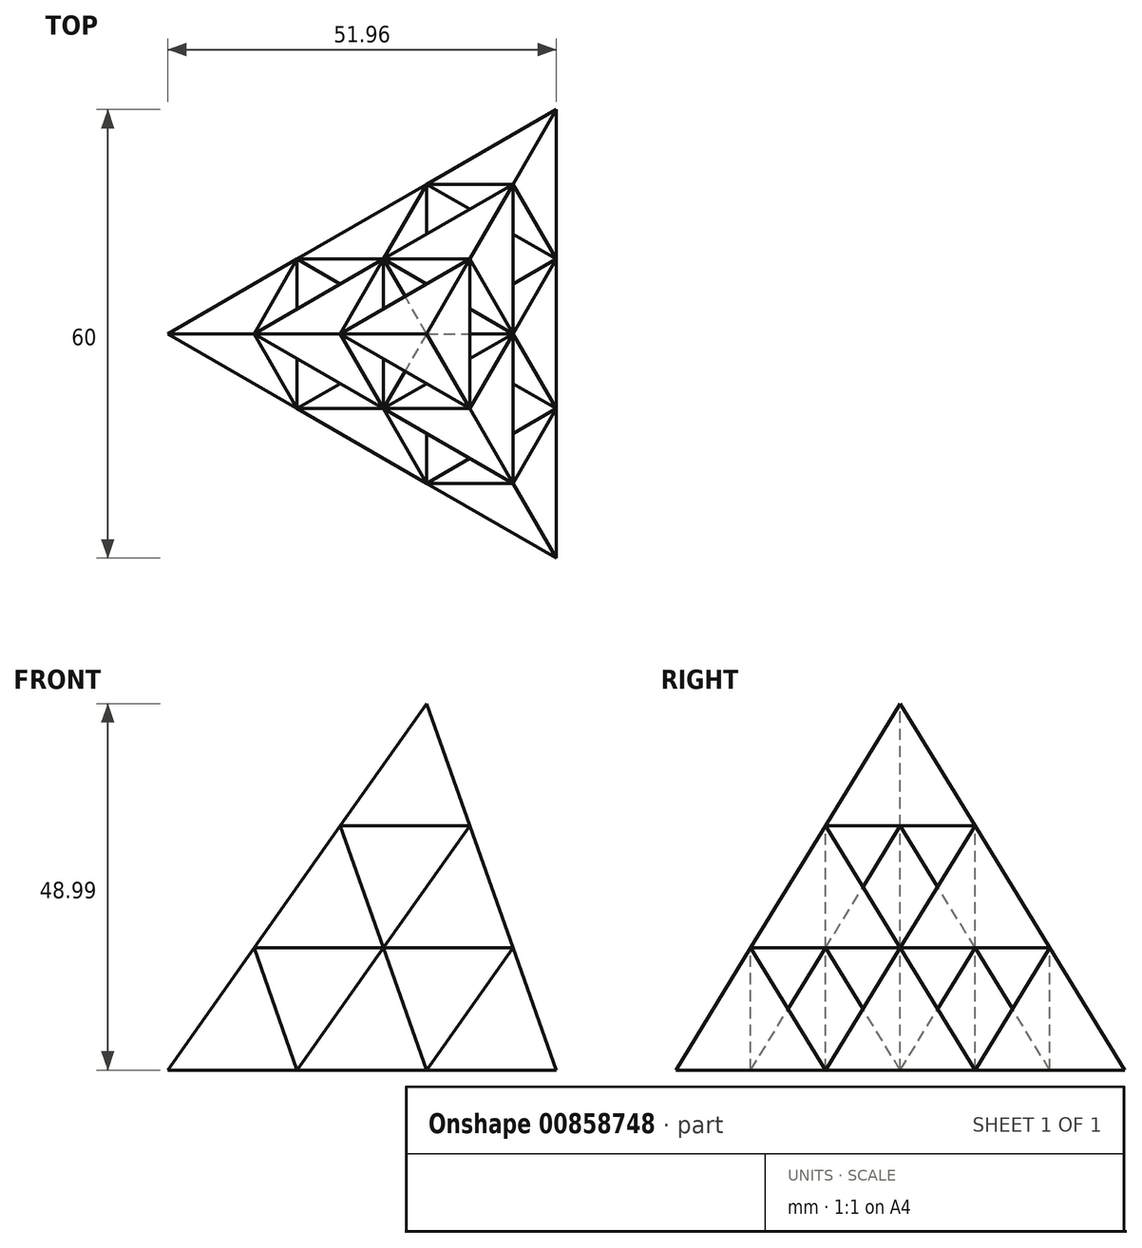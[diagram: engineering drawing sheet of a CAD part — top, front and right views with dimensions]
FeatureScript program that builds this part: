
annotation { "Feature Type Name" : "Feature", "Feature Type Description" : "" }
export const myFeature = defineFeature(function(context is Context, id is Id, definition is map)
    precondition{}
    {
        {
            var Q0;
            Q0=qCreatedBy(makeId("Top.planeOp"),FACE);
            var sketch = newSketch(context, id + "F0", { "sketchPlane" : qUnion([Q0])});
            skCircle(sketch, "E0.cCircle", {"center": v(0, 0) * mm, "radius": 5.77 * mm, "construction": true});
            skLineSegment(sketch, "E0.0", {"start": v(5.77, 10) * mm, "end": v(5.77, -10) * mm});
            skLineSegment(sketch, "E0.1", {"start": v(5.77, -10) * mm, "end": v(-11.55, 0) * mm});
            skLineSegment(sketch, "E0.2", {"start": v(-11.55, 0) * mm, "end": v(5.77, 10) * mm});
            skPoint(sketch, "E0.0.midPoint", {"position": v(5.77, 0) * mm});
            skSolve(sketch);
        }
        {
            var Q0;
            Q0=qCreatedBy(makeId("Front.planeOp"),FACE);
            var sketch = newSketch(context, id + "F1", { "sketchPlane" : qUnion([Q0])});
            skLineSegment(sketch, "E1", {"start": v(-11.55, 0) * mm, "end": v(0, 16.33) * mm});
            skSolve(sketch);
        }
        {
            var Q0;
            Q0=makeQuery(id+"F0.imprint","IMPRINT",FACE,{"disambiguationData":[TD([[makeQuery(id+"F0.imprint","IMPRINT",EDGE,{"derivedFrom":sQuery(id+"F0.wireOp",EDGE,"E0.0")}),-1.0]])]});
            var Q1;
            Q1=sQuery(id+"F1.wireOp",VERTEX,"E1.end");
            loft(context, id + "F2", {"sheetProfilesArray" : [{ "sheetProfileEntities" : qUnion([Q0]) }, { "sheetProfileEntities" : qUnion([Q1]) }]});
        }
        {
            var Q0;
            Q0=makeQuery(id+"F2.opLoft","SWEPT_BODY",BODY,{"disambiguationData":[OSD([makeQuery(id+"F0.imprint","IMPRINT",FACE,{"disambiguationData":[TD([[makeQuery(id+"F0.imprint","IMPRINT",EDGE,{"derivedFrom":sQuery(id+"F0.wireOp",EDGE,"E0.0")}),-1.0]])]}),sQuery(id+"F1.wireOp",VERTEX,"E1.end")])]});
            var Q1;
            Q1=makeQuery(id+"F2.opLoft","SWEPT_EDGE",EDGE,{"disambiguationData":[OSD([sQuery(id+"F0.wireOp",EDGE,"E0.0"),sQuery(id+"F0.wireOp",EDGE,"E0.1"),sQuery(id+"F1.wireOp",VERTEX,"E1.end")])]});
            transform(context, id + "F3", {"entities" : qUnion([Q0]), "transformType" : TransformType.TRANSLATION_ENTITY, "oppositeDirectionEntity" : true, "transformLine" : qUnion([Q1]), "makeCopy" : true});
        }
        {
            var Q0;
            Q0=makeQuery(id+"F2.opLoft","SWEPT_BODY",BODY,{"disambiguationData":[OSD([makeQuery(id+"F0.imprint","IMPRINT",FACE,{"disambiguationData":[TD([[makeQuery(id+"F0.imprint","IMPRINT",EDGE,{"derivedFrom":sQuery(id+"F0.wireOp",EDGE,"E0.0")}),-1.0]])]}),sQuery(id+"F1.wireOp",VERTEX,"E1.end")])]});
            var Q1;
            Q1=makeQuery(id+"F2.opLoft","SWEPT_EDGE",EDGE,{"disambiguationData":[OSD([sQuery(id+"F0.wireOp",EDGE,"E0.0"),sQuery(id+"F0.wireOp",EDGE,"E0.2"),sQuery(id+"F1.wireOp",VERTEX,"E1.end")])]});
            transform(context, id + "F4", {"entities" : qUnion([Q0]), "transformType" : TransformType.TRANSLATION_ENTITY, "oppositeDirectionEntity" : true, "transformLine" : qUnion([Q1]), "makeCopy" : true});
        }
        {
            var Q0;
            Q0=makeQuery(id+"F2.opLoft","SWEPT_BODY",BODY,{"disambiguationData":[OSD([makeQuery(id+"F0.imprint","IMPRINT",FACE,{"disambiguationData":[TD([[makeQuery(id+"F0.imprint","IMPRINT",EDGE,{"derivedFrom":sQuery(id+"F0.wireOp",EDGE,"E0.0")}),-1.0]])]}),sQuery(id+"F1.wireOp",VERTEX,"E1.end")])]});
            var Q1;
            Q1=makeQuery(id+"F2.opLoft","SWEPT_EDGE",EDGE,{"disambiguationData":[OSD([sQuery(id+"F0.wireOp",EDGE,"E0.1"),sQuery(id+"F0.wireOp",EDGE,"E0.2"),sQuery(id+"F1.wireOp",VERTEX,"E1.end")])]});
            transform(context, id + "F5", {"entities" : qUnion([Q0]), "transformType" : TransformType.TRANSLATION_ENTITY, "oppositeDirectionEntity" : true, "transformLine" : qUnion([Q1]), "makeCopy" : true});
        }
        {
            var Q0;
            Q0=makeQuery(id+"F3.opPattern","COPY",BODY,{"derivedFrom":makeQuery(id+"F2.opLoft","SWEPT_BODY",BODY,{"disambiguationData":[OSD([makeQuery(id+"F0.imprint","IMPRINT",FACE,{"disambiguationData":[TD([[makeQuery(id+"F0.imprint","IMPRINT",EDGE,{"derivedFrom":sQuery(id+"F0.wireOp",EDGE,"E0.0")}),-1.0]])]}),sQuery(id+"F1.wireOp",VERTEX,"E1.end")])]}),"instanceName":"1"});
            var Q1;
            Q1=makeQuery(id+"F4.opPattern","COPY",BODY,{"derivedFrom":makeQuery(id+"F2.opLoft","SWEPT_BODY",BODY,{"disambiguationData":[OSD([makeQuery(id+"F0.imprint","IMPRINT",FACE,{"disambiguationData":[TD([[makeQuery(id+"F0.imprint","IMPRINT",EDGE,{"derivedFrom":sQuery(id+"F0.wireOp",EDGE,"E0.0")}),-1.0]])]}),sQuery(id+"F1.wireOp",VERTEX,"E1.end")])]}),"instanceName":"1"});
            var Q2;
            Q2=makeQuery(id+"F5.opPattern","COPY",BODY,{"derivedFrom":makeQuery(id+"F2.opLoft","SWEPT_BODY",BODY,{"disambiguationData":[OSD([makeQuery(id+"F0.imprint","IMPRINT",FACE,{"disambiguationData":[TD([[makeQuery(id+"F0.imprint","IMPRINT",EDGE,{"derivedFrom":sQuery(id+"F0.wireOp",EDGE,"E0.0")}),-1.0]])]}),sQuery(id+"F1.wireOp",VERTEX,"E1.end")])]}),"instanceName":"1"});
            var Q3;
            Q3=makeQuery(id+"F5.opPattern","COPY",EDGE,{"derivedFrom":makeQuery(id+"F2.opLoft","SWEPT_EDGE",EDGE,{"disambiguationData":[OSD([sQuery(id+"F0.wireOp",EDGE,"E0.1"),sQuery(id+"F0.wireOp",EDGE,"E0.2"),sQuery(id+"F1.wireOp",VERTEX,"E1.end")])]}),"instanceName":"1"});
            transform(context, id + "F6", {"entities" : qUnion([Q0, Q1, Q2]), "transformType" : TransformType.TRANSLATION_ENTITY, "oppositeDirectionEntity" : true, "transformLine" : qUnion([Q3]), "makeCopy" : true});
        }
        {
            var Q0;
            Q0=makeQuery(id+"F5.opPattern","COPY",BODY,{"derivedFrom":makeQuery(id+"F2.opLoft","SWEPT_BODY",BODY,{"disambiguationData":[OSD([makeQuery(id+"F0.imprint","IMPRINT",FACE,{"disambiguationData":[TD([[makeQuery(id+"F0.imprint","IMPRINT",EDGE,{"derivedFrom":sQuery(id+"F0.wireOp",EDGE,"E0.0")}),-1.0]])]}),sQuery(id+"F1.wireOp",VERTEX,"E1.end")])]}),"instanceName":"1"});
            var Q1;
            Q1=makeQuery(id+"F4.opPattern","COPY",BODY,{"derivedFrom":makeQuery(id+"F2.opLoft","SWEPT_BODY",BODY,{"disambiguationData":[OSD([makeQuery(id+"F0.imprint","IMPRINT",FACE,{"disambiguationData":[TD([[makeQuery(id+"F0.imprint","IMPRINT",EDGE,{"derivedFrom":sQuery(id+"F0.wireOp",EDGE,"E0.0")}),-1.0]])]}),sQuery(id+"F1.wireOp",VERTEX,"E1.end")])]}),"instanceName":"1"});
            var Q2;
            Q2=makeQuery(id+"F3.opPattern","COPY",BODY,{"derivedFrom":makeQuery(id+"F2.opLoft","SWEPT_BODY",BODY,{"disambiguationData":[OSD([makeQuery(id+"F0.imprint","IMPRINT",FACE,{"disambiguationData":[TD([[makeQuery(id+"F0.imprint","IMPRINT",EDGE,{"derivedFrom":sQuery(id+"F0.wireOp",EDGE,"E0.0")}),-1.0]])]}),sQuery(id+"F1.wireOp",VERTEX,"E1.end")])]}),"instanceName":"1"});
            var Q3;
            Q3=makeQuery(id+"F3.opPattern","COPY",EDGE,{"derivedFrom":makeQuery(id+"F2.opLoft","SWEPT_EDGE",EDGE,{"disambiguationData":[OSD([sQuery(id+"F0.wireOp",EDGE,"E0.0"),sQuery(id+"F0.wireOp",EDGE,"E0.1"),sQuery(id+"F1.wireOp",VERTEX,"E1.end")])]}),"instanceName":"1"});
            transform(context, id + "F7", {"entities" : qUnion([Q0, Q1, Q2]), "transformType" : TransformType.TRANSLATION_ENTITY, "oppositeDirectionEntity" : true, "transformLine" : qUnion([Q3]), "makeCopy" : true});
        }
        {
            var Q0;
            Q0=makeQuery(id+"F4.opPattern","COPY",BODY,{"derivedFrom":makeQuery(id+"F2.opLoft","SWEPT_BODY",BODY,{"disambiguationData":[OSD([makeQuery(id+"F0.imprint","IMPRINT",FACE,{"disambiguationData":[TD([[makeQuery(id+"F0.imprint","IMPRINT",EDGE,{"derivedFrom":sQuery(id+"F0.wireOp",EDGE,"E0.0")}),-1.0]])]}),sQuery(id+"F1.wireOp",VERTEX,"E1.end")])]}),"instanceName":"1"});
            var Q1;
            Q1=makeQuery(id+"F4.opPattern","COPY",EDGE,{"derivedFrom":makeQuery(id+"F2.opLoft","SWEPT_EDGE",EDGE,{"disambiguationData":[OSD([sQuery(id+"F0.wireOp",EDGE,"E0.0"),sQuery(id+"F0.wireOp",EDGE,"E0.2"),sQuery(id+"F1.wireOp",VERTEX,"E1.end")])]}),"instanceName":"1"});
            transform(context, id + "F8", {"entities" : qUnion([Q0]), "transformType" : TransformType.TRANSLATION_ENTITY, "oppositeDirectionEntity" : true, "transformLine" : qUnion([Q1]), "makeCopy" : true});
        }
    });
